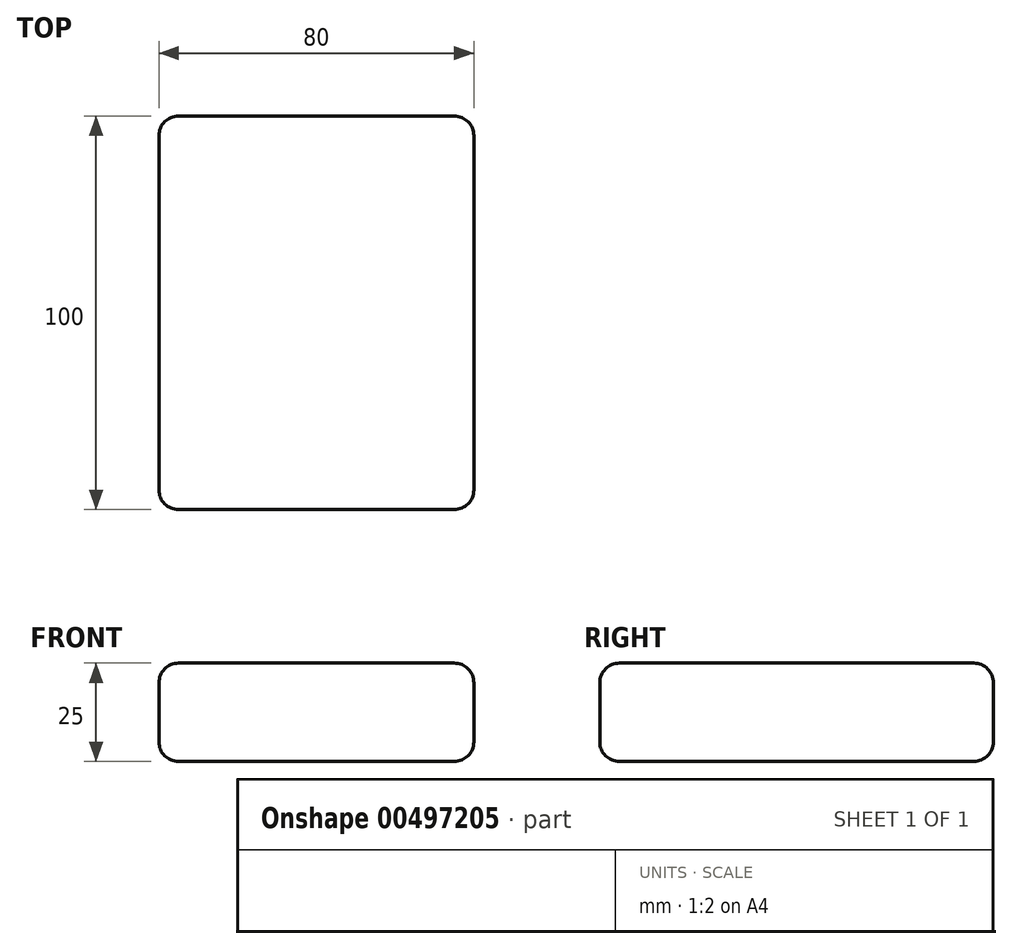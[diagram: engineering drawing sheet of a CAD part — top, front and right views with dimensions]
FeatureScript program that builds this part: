
annotation { "Feature Type Name" : "Feature", "Feature Type Description" : "" }
export const myFeature = defineFeature(function(context is Context, id is Id, definition is map)
    precondition{}
    {
        {
            var Q0;
            Q0=qCreatedBy(makeId("Top.planeOp"),FACE);
            var sketch = newSketch(context, id + "F0", { "sketchPlane" : qUnion([Q0])});
            skLineSegment(sketch, "E0.bottom", {"start": v(-40, 50) * mm, "end": v(40, 50) * mm});
            skLineSegment(sketch, "E0.top", {"start": v(-40, -50) * mm, "end": v(40, -50) * mm});
            skLineSegment(sketch, "E0.left", {"start": v(-40, 50) * mm, "end": v(-40, -50) * mm});
            skLineSegment(sketch, "E0.right", {"start": v(40, 50) * mm, "end": v(40, -50) * mm});
            skPoint(sketch, "E0.middle", {"position": v(0, 0) * mm});
            skSolve(sketch);
        }
        {
            var Q0;
            Q0=makeQuery(id+"F0.imprint","IMPRINT",FACE,{"disambiguationData":[TD([[makeQuery(id+"F0.imprint","IMPRINT",EDGE,{"derivedFrom":sQuery(id+"F0.wireOp",EDGE,"E0.bottom")}),-1.0]])]});
            extrude(context, id + "F1", {"entities" : qUnion([Q0]), "depth" : 25 * mm});
        }
        {
            var Q0;
            Q0=makeQuery(id+"F1.opExtrude","SWEPT_EDGE",EDGE,{"disambiguationData":[OSD([sQuery(id+"F0.wireOp",EDGE,"E0.top"),sQuery(id+"F0.wireOp",EDGE,"E0.right")])]});
            var Q1;
            Q1=makeQuery(id+"F1.opExtrude","SWEPT_EDGE",EDGE,{"disambiguationData":[OSD([sQuery(id+"F0.wireOp",EDGE,"E0.top"),sQuery(id+"F0.wireOp",EDGE,"E0.left")])]});
            var Q2;
            Q2=makeQuery(id+"F1.opExtrude","CAP_EDGE",EDGE,{"disambiguationData":[OSD([sQuery(id+"F0.wireOp",EDGE,"E0.top")])],"isStart":true});
            var Q3;
            Q3=makeQuery(id+"F1.opExtrude","CAP_EDGE",EDGE,{"disambiguationData":[OSD([sQuery(id+"F0.wireOp",EDGE,"E0.top")])],"isStart":false});
            var Q4;
            Q4=makeQuery(id+"F1.opExtrude","CAP_EDGE",EDGE,{"disambiguationData":[OSD([sQuery(id+"F0.wireOp",EDGE,"E0.left")])],"isStart":false});
            var Q5;
            Q5=makeQuery(id+"F1.opExtrude","CAP_EDGE",EDGE,{"disambiguationData":[OSD([sQuery(id+"F0.wireOp",EDGE,"E0.right")])],"isStart":false});
            var Q6;
            Q6=makeQuery(id+"F1.opExtrude","CAP_EDGE",EDGE,{"disambiguationData":[OSD([sQuery(id+"F0.wireOp",EDGE,"E0.bottom")])],"isStart":false});
            var Q7;
            Q7=makeQuery(id+"F1.opExtrude","CAP_EDGE",EDGE,{"disambiguationData":[OSD([sQuery(id+"F0.wireOp",EDGE,"E0.right")])],"isStart":true});
            var Q8;
            Q8=makeQuery(id+"F1.opExtrude","SWEPT_EDGE",EDGE,{"disambiguationData":[OSD([sQuery(id+"F0.wireOp",EDGE,"E0.bottom"),sQuery(id+"F0.wireOp",EDGE,"E0.right")])]});
            var Q9;
            Q9=makeQuery(id+"F1.opExtrude","CAP_EDGE",EDGE,{"disambiguationData":[OSD([sQuery(id+"F0.wireOp",EDGE,"E0.bottom")])],"isStart":true});
            var Q10;
            Q10=makeQuery(id+"F1.opExtrude","SWEPT_EDGE",EDGE,{"disambiguationData":[OSD([sQuery(id+"F0.wireOp",EDGE,"E0.bottom"),sQuery(id+"F0.wireOp",EDGE,"E0.left")])]});
            var Q11;
            Q11=makeQuery(id+"F1.opExtrude","CAP_EDGE",EDGE,{"disambiguationData":[OSD([sQuery(id+"F0.wireOp",EDGE,"E0.left")])],"isStart":true});
            fillet(context, id + "F2", {"entities" : qUnion([Q0, Q1, Q2, Q3, Q4, Q5, Q6, Q7, Q8, Q9, Q10, Q11]), "radius" : 5 * mm, "tangentPropagation" : true, "allowEdgeOverflow" : false});
        }
    });
